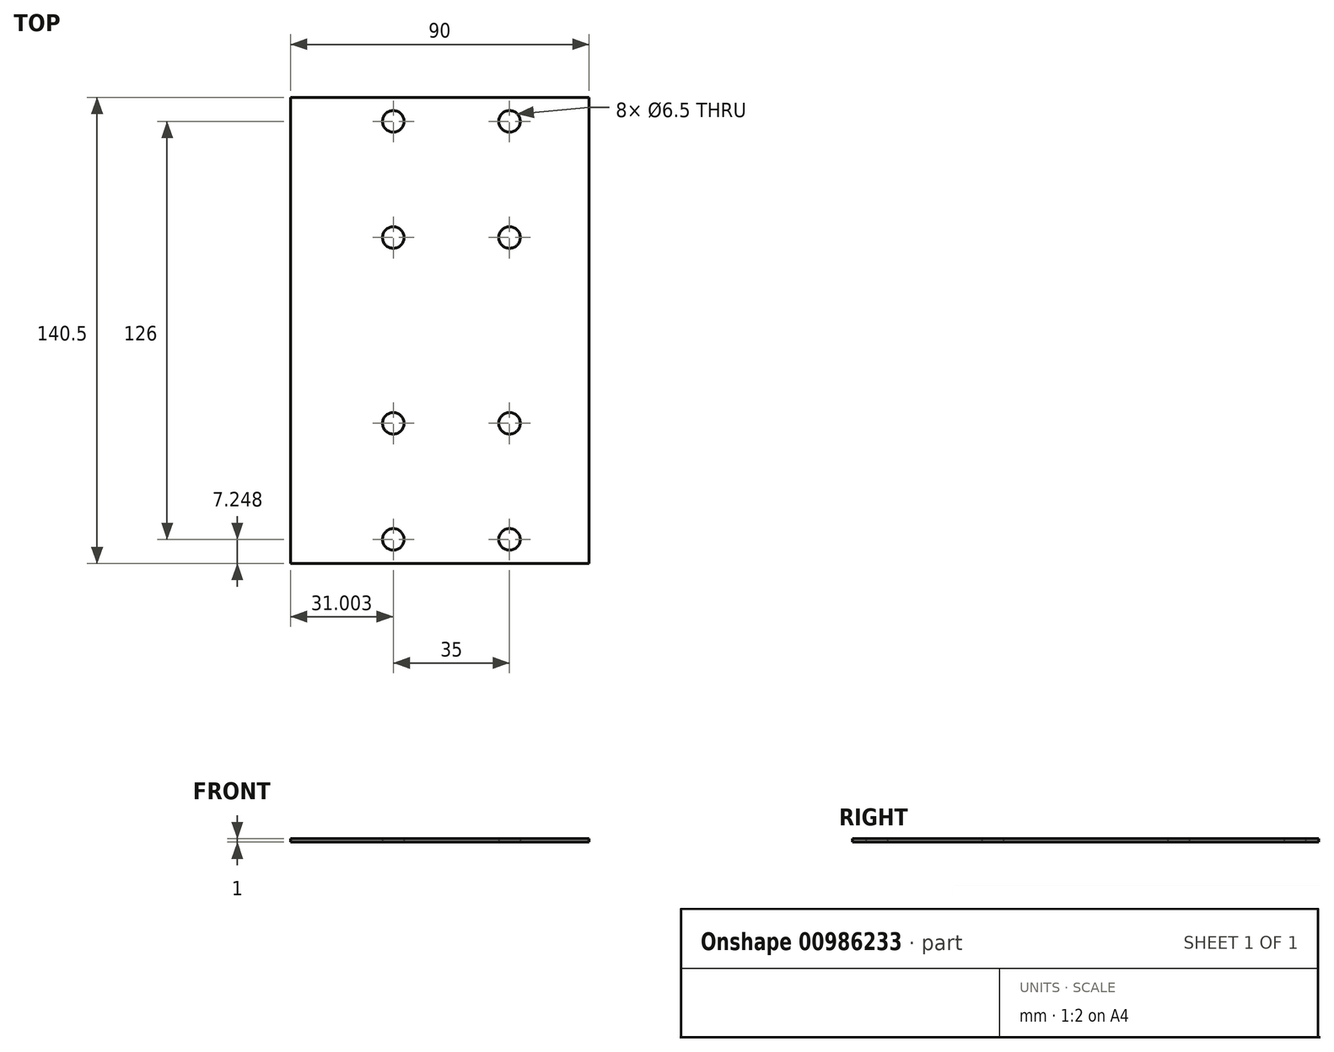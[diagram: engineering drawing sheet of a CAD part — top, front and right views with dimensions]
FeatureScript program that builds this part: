
annotation { "Feature Type Name" : "Feature", "Feature Type Description" : "" }
export const myFeature = defineFeature(function(context is Context, id is Id, definition is map)
    precondition{}
    {
        {
            var Q0;
            Q0=qCreatedBy(makeId("Top.planeOp"),FACE);
            var sketch = newSketch(context, id + "F0", { "sketchPlane" : qUnion([Q0])});
            skLineSegment(sketch, "E0.bottom", {"start": v(-53.24, 129.68) * mm, "end": v(36.76, 129.68) * mm});
            skLineSegment(sketch, "E0.top", {"start": v(-53.24, -10.82) * mm, "end": v(36.76, -10.82) * mm});
            skLineSegment(sketch, "E0.left", {"start": v(-53.24, 129.68) * mm, "end": v(-53.24, -10.82) * mm});
            skLineSegment(sketch, "E0.right", {"start": v(36.76, 129.68) * mm, "end": v(36.76, -10.82) * mm});
            skCircle(sketch, "E1", {"center": v(-22.24, 122.43) * mm, "radius": 3.25 * mm});
            skCircle(sketch, "E2", {"center": v(-22.24, 87.43) * mm, "radius": 3.25 * mm});
            skCircle(sketch, "E3", {"center": v(12.76, 122.43) * mm, "radius": 3.25 * mm});
            skCircle(sketch, "E4", {"center": v(12.76, 87.43) * mm, "radius": 3.25 * mm});
            skCircle(sketch, "E5", {"center": v(-22.24, 31.43) * mm, "radius": 3.25 * mm});
            skCircle(sketch, "E6", {"center": v(-22.24, -3.57) * mm, "radius": 3.25 * mm});
            skCircle(sketch, "E7", {"center": v(12.76, 31.43) * mm, "radius": 3.25 * mm});
            skCircle(sketch, "E8", {"center": v(12.76, -3.57) * mm, "radius": 3.25 * mm});
            skLineSegment(sketch, "E9", {"start": v(12.76, 122.43) * mm, "end": v(12.76, 129.68) * mm, "construction": true});
            skLineSegment(sketch, "E10", {"start": v(12.76, -3.57) * mm, "end": v(12.76, -10.82) * mm, "construction": true});
            skSolve(sketch);
        }
        {
            var Q0;
            Q0=makeQuery(id+"F0.imprint","IMPRINT",FACE,{"disambiguationData":[TD([[makeQuery(id+"F0.imprint","IMPRINT",EDGE,{"derivedFrom":sQuery(id+"F0.wireOp",EDGE,"E0.bottom")}),-1.0]])]});
            extrude(context, id + "F1", {"entities" : qUnion([Q0]), "depth" : 1 * mm, "offsetDistance" : 25 * mm});
        }
    });
